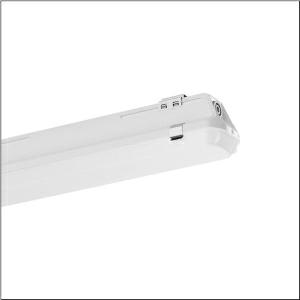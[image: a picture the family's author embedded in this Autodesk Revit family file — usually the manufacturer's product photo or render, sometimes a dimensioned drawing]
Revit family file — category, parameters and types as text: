
# Revit family: monsun_r__21_emergency_51fb20dp467b3h_0bb8
name_source: partatom
category: Lighting Fixtures
units: mm (PartAtom-declared; Revit-internal decimal feet)

## family parameters
Cut with Voids When Loaded = No
Host = Face
Light Source = No
Part Type = Normal
Room Calculation Point = No
Round Connector Dimension = Use Diameter
Shared = No

## types (1)
- --- (1 x LED, 5460 lm, 42.2 W, 4000K)
    Apparent Load = 42 VA
    CIE Flux Codes = 45 75 93 94 100
    Color Rendering = 80
    Color Temperature = 4000K
    Default Elevation = 1800 mm
    Description = Monsun® 21 emergency, damp-proof luminaire, chain hanger, primary optical cover: enclosure, of PC, light emission: direct distribution, primary light characteristic: symmetric, installation type: vertical mounting, horizontal mounting, surface-mounted, suspended mounting, LED, rated luminous flux: 5.460lm, luminous efficacy: 129lm/W, light colour: 840, colour temperature: 4000K, control gear: ECG DALI, with terminal, 5+3-pole, max. 2.5mm², mains connection: 220..240V, AC, 50/60Hz, rated input power: 42W, control gear: single battery element, battery: NiCd, 4,5Ah, mains connection: 230V, housing, of glass-fibre reinforced polyester, uncoated, bright grey, incl. chain hanger, length: 1.590mm, width: 90mm, height: 88mm, clip for enclosure, of stainless steel (V2A), ceiling mounting element, of stainless steel (V2A), chain hanger, of stainless steel (V2A), protection rating (complete): IP66, insulation class (complete): insulation class I (protective earthing), certification: CE, UKCA, protection symbol: D, impact resistance: IK08, permissible operating ambient temperature: +5..+25°C, standard: EN 60598-2-1, EN 50419, EN 60598-2-22, corresponds to IFS (International Featured Standards) requirements for safety and quality in the food industry, for indoor or canopied outdoor use, no direct snow, no direct sun, no direct rain, contact your sales advisor before using the luminaires in applications with unclear chemical exposure, large temperature fluctuations or condensation-forming humidity, LABS conformity tested according to VDMA 24364:2018-05, packaging unit: 1 piece
    Height = 89 mm
    Lamp = 1 x LED
    Lamp Light Flux = 5460 lm
    Lamp Power = 42.2 W
    Lamp count = 1
    Length = 1590 mm
    Luminous efficacy = 129 lm/W
    Manufacturer = Siteco
    ModVariant = No
    Model = 51FB20DP467B3H
    Mounting Place = Ceiling
    Mounting Type = Surface mounted
    Number of Poles = 1
    OnlyDefault = Yes
    Power Factor = 1
    Product Name = Monsun® 21 emergency
    Product group = damp-proof luminaire
    ProductGroupID = 301
    Protection Class = Protection class I
    Protection Degree = IP 66
    RLX_Detail_Level = 1
    RLX_Emergency_Light_Flux = 0 lm
    RLX_Emergency_Type = 0
    RLX_Emergency_Type_DB = No
    RlxData = <blob elided: 92321 chars, md5=164ff2d6>
    Socket = socket
    Standby Power = 0 W
    System Light Flux = 5460 lm
    System Power = 42 W
    Type Comments = factory setting: luminous flux: 100 % | dim-lin: 254 | 261 mA
    Type Image = l_1006717.jpg
    URL = http://relux.com
    VarID = @adj_151907
    Voltage = 0 V
    Weight = 0.00 kg
    Width = 90 mm

## geometry (parser evidence)
native form markers: Blend x4, Sweep x14
no freeform markers — native parametric forms only
